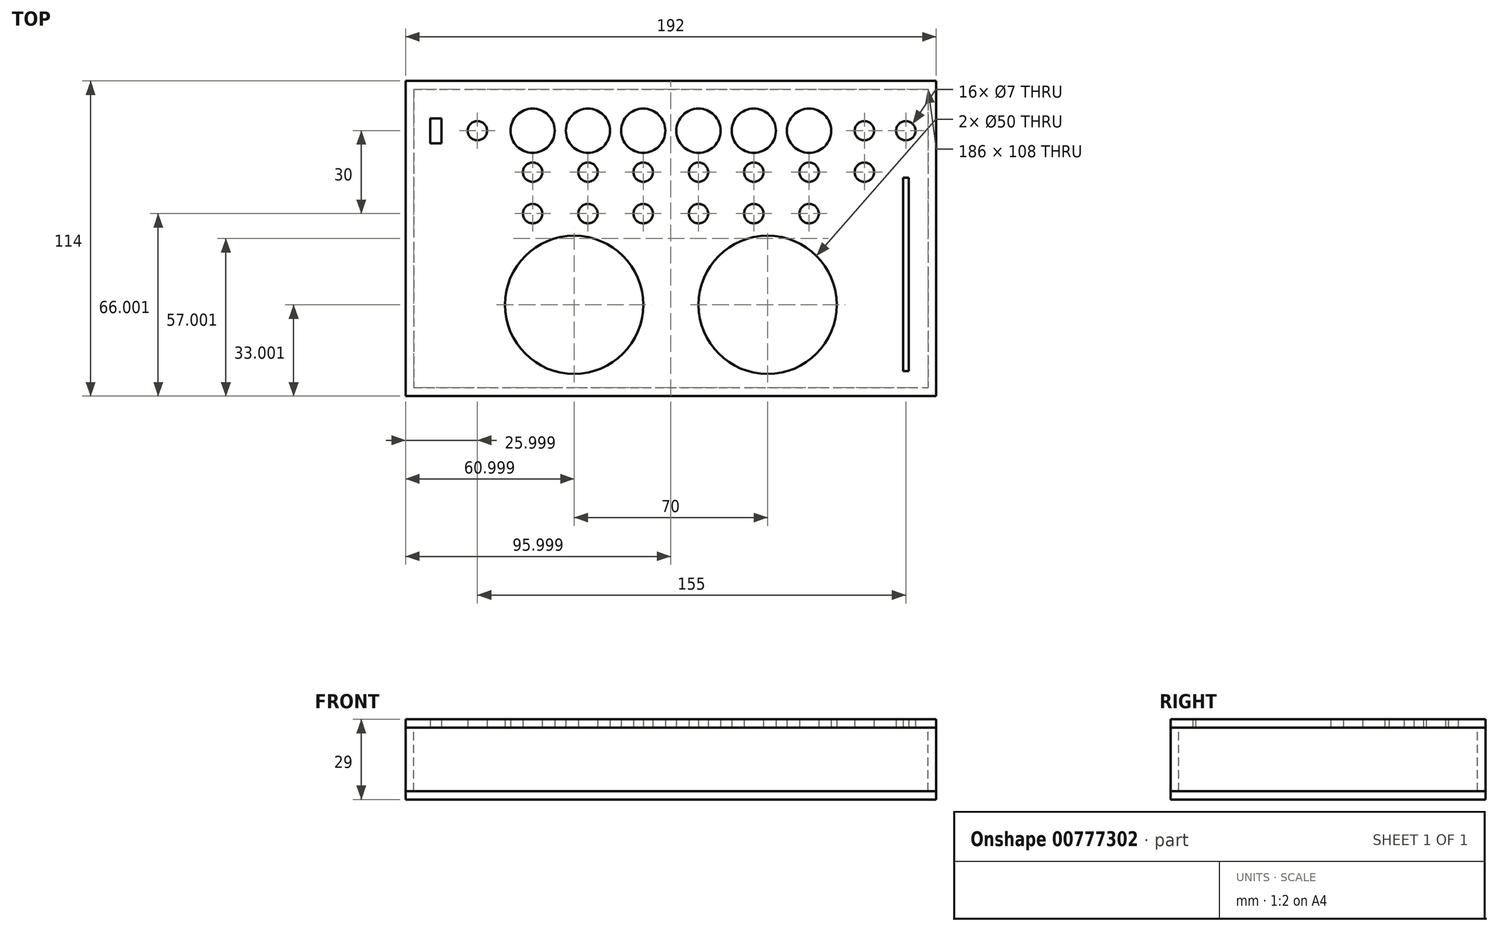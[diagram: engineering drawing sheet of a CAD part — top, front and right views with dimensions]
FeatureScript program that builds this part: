
annotation { "Feature Type Name" : "Feature", "Feature Type Description" : "" }
export const myFeature = defineFeature(function(context is Context, id is Id, definition is map)
    precondition{}
    {
        {
            assignVariable(context, id + "F0", {"name" : "Thickness", "anyValue" : 3});
        }
        {
            var Q0;
            Q0=qCreatedBy(makeId("Top.planeOp"),FACE);
            var sketch = newSketch(context, id + "F1", { "sketchPlane" : qUnion([Q0])});
            skLineSegment(sketch, "E0.bottom", {"start": v(-101.05, 57.8) * mm, "end": v(90.95, 57.8) * mm});
            skLineSegment(sketch, "E0.top", {"start": v(-101.05, -56.2) * mm, "end": v(90.95, -56.2) * mm});
            skLineSegment(sketch, "E0.left", {"start": v(-101.05, 57.8) * mm, "end": v(-101.05, -56.2) * mm});
            skLineSegment(sketch, "E0.right", {"start": v(90.95, 57.8) * mm, "end": v(90.95, -56.2) * mm});
            skLineSegment(sketch, "E1.0", {"start": v(-98.05, 54.8) * mm, "end": v(-98.05, -53.2) * mm});
            skLineSegment(sketch, "E1.1", {"start": v(-98.05, 54.8) * mm, "end": v(87.95, 54.8) * mm});
            skLineSegment(sketch, "E1.2", {"start": v(87.95, 54.8) * mm, "end": v(87.95, -53.2) * mm});
            skLineSegment(sketch, "E1.3", {"start": v(-98.05, -53.2) * mm, "end": v(87.95, -53.2) * mm});
            skLineSegment(sketch, "E2.bottom", {"start": v(73.45, -6.8) * mm, "end": v(56.45, -6.8) * mm});
            skLineSegment(sketch, "E2.top", {"start": v(73.45, 13.2) * mm, "end": v(56.45, 13.2) * mm});
            skLineSegment(sketch, "E2.left", {"start": v(73.45, -6.8) * mm, "end": v(73.45, 13.2) * mm});
            skLineSegment(sketch, "E2.right", {"start": v(56.45, -6.8) * mm, "end": v(56.45, 13.2) * mm});
            skPoint(sketch, "E2.middle", {"position": v(64.95, 3.2) * mm});
            skLineSegment(sketch, "E3.bottom", {"start": v(-88.05, 35.3) * mm, "end": v(-92.05, 35.3) * mm});
            skLineSegment(sketch, "E3.top", {"start": v(-88.05, 44.3) * mm, "end": v(-92.05, 44.3) * mm});
            skLineSegment(sketch, "E3.left", {"start": v(-88.05, 35.3) * mm, "end": v(-88.05, 44.3) * mm});
            skLineSegment(sketch, "E3.right", {"start": v(-92.05, 35.3) * mm, "end": v(-92.05, 44.3) * mm});
            skPoint(sketch, "E3.middle", {"position": v(-90.05, 39.8) * mm});
            skCircle(sketch, "E4", {"center": v(-75.05, 39.8) * mm, "radius": 3.5 * mm});
            skLineSegment(sketch, "E5.bottom", {"start": v(84.95, -49.72) * mm, "end": v(74.95, -49.72) * mm});
            skLineSegment(sketch, "E5.top", {"start": v(84.95, 25.28) * mm, "end": v(74.95, 25.28) * mm});
            skLineSegment(sketch, "E5.left", {"start": v(84.95, -49.72) * mm, "end": v(84.95, 25.28) * mm});
            skLineSegment(sketch, "E5.right", {"start": v(74.95, -49.72) * mm, "end": v(74.95, 25.28) * mm});
            skLineSegment(sketch, "E6.bottom", {"start": v(80.95, -47.22) * mm, "end": v(78.95, -47.22) * mm});
            skLineSegment(sketch, "E6.top", {"start": v(80.95, 22.78) * mm, "end": v(78.95, 22.78) * mm});
            skLineSegment(sketch, "E6.left", {"start": v(80.95, -47.22) * mm, "end": v(80.95, 22.78) * mm});
            skLineSegment(sketch, "E6.right", {"start": v(78.95, -47.22) * mm, "end": v(78.95, 22.78) * mm});
            skPoint(sketch, "E6.middle", {"position": v(79.95, -12.22) * mm});
            skCircle(sketch, "E7", {"center": v(79.95, 39.8) * mm, "radius": 3.5 * mm});
            skCircle(sketch, "E8", {"center": v(4.95, 39.8) * mm, "radius": 8 * mm});
            skCircle(sketch, "E9", {"center": v(-15.05, 39.8) * mm, "radius": 8 * mm});
            skCircle(sketch, "E10", {"center": v(24.95, 39.8) * mm, "radius": 8 * mm});
            skCircle(sketch, "E11", {"center": v(4.95, 24.8) * mm, "radius": 3.5 * mm});
            skCircle(sketch, "E12", {"center": v(44.95, 24.8) * mm, "radius": 3.5 * mm});
            skCircle(sketch, "E13", {"center": v(24.95, 24.8) * mm, "radius": 3.5 * mm});
            skCircle(sketch, "E14", {"center": v(-35.05, 24.8) * mm, "radius": 3.5 * mm});
            skCircle(sketch, "E15", {"center": v(-15.05, 24.8) * mm, "radius": 3.5 * mm});
            skCircle(sketch, "E16", {"center": v(-55.05, 24.8) * mm, "radius": 3.5 * mm});
            skCircle(sketch, "E17", {"center": v(24.95, 9.8) * mm, "radius": 3.5 * mm});
            skCircle(sketch, "E18", {"center": v(44.95, 9.8) * mm, "radius": 3.5 * mm});
            skCircle(sketch, "E19", {"center": v(4.95, 9.8) * mm, "radius": 3.5 * mm});
            skCircle(sketch, "E20", {"center": v(-35.05, 9.8) * mm, "radius": 3.5 * mm});
            skCircle(sketch, "E21", {"center": v(-15.05, 9.8) * mm, "radius": 3.5 * mm});
            skCircle(sketch, "E22", {"center": v(-55.05, 9.8) * mm, "radius": 3.5 * mm});
            skCircle(sketch, "E23", {"center": v(64.95, 39.8) * mm, "radius": 3.5 * mm});
            skCircle(sketch, "E24", {"center": v(64.95, 24.8) * mm, "radius": 3.5 * mm});
            skCircle(sketch, "E25", {"center": v(-35.05, 39.8) * mm, "radius": 8 * mm});
            skCircle(sketch, "E26", {"center": v(44.95, 39.8) * mm, "radius": 8 * mm});
            skCircle(sketch, "E27", {"center": v(-55.05, 39.8) * mm, "radius": 8 * mm});
            skCircle(sketch, "E28", {"center": v(-40.05, -23.2) * mm, "radius": 25 * mm});
            skCircle(sketch, "E29", {"center": v(29.95, -23.2) * mm, "radius": 25 * mm});
            skSolve(sketch);
        }
        {
            var Q0;
            Q0=makeQuery(id+"F1.imprint","IMPRINT",FACE,{"disambiguationData":[TD([[makeQuery(id+"F1.imprint","IMPRINT",EDGE,{"derivedFrom":sQuery(id+"F1.wireOp",EDGE,"E0.bottom")}),-1.0]])]});
            extrude(context, id + "F2", {"entities" : qUnion([Q0]), "oppositeDirection" : true, "depth" : (29 - getVariable(context, 'Thickness') * 2) * mm, "offsetDistance" : 25 * mm});
        }
        {
            var Q0;
            Q0=makeQuery(id+"F1.imprint","IMPRINT",FACE,{"disambiguationData":[TD([[makeQuery(id+"F1.imprint","IMPRINT",EDGE,{"derivedFrom":sQuery(id+"F1.wireOp",EDGE,"E0.bottom")}),-1.0]])]});
            var Q1;
            Q1=makeQuery(id+"F1.imprint","IMPRINT",FACE,{"disambiguationData":[TD([[makeQuery(id+"F1.imprint","IMPRINT",EDGE,{"derivedFrom":sQuery(id+"F1.wireOp",EDGE,"E1.0")}),1.0]])]});
            var Q2;
            Q2=makeQuery(id+"F1.imprint","IMPRINT",FACE,{"disambiguationData":[TD([[makeQuery(id+"F1.imprint","IMPRINT",EDGE,{"derivedFrom":sQuery(id+"F1.wireOp",EDGE,"E2.bottom")}),-1.0]])]});
            var Q3;
            Q3=makeQuery(id+"F1.imprint","IMPRINT",FACE,{"disambiguationData":[TD([[makeQuery(id+"F1.imprint","IMPRINT",EDGE,{"derivedFrom":sQuery(id+"F1.wireOp",EDGE,"E5.bottom")}),-1.0]])]});
            var Q4;
            Q4=makeQuery(id+"F1.imprint","IMPRINT",FACE,{"disambiguationData":[TD([[makeQuery(id+"F1.imprint","IMPRINT",EDGE,{"derivedFrom":sQuery(id+"F1.wireOp",EDGE,"1PGvYNiY-SpdE-KHsO-0nZL-MrIaACnWbyKp.bottom")}),-1.0]])]});
            extrude(context, id + "F3", {"entities" : qUnion([Q0, Q1, Q2, Q3, Q4]), "depth" : (getVariable(context, 'Thickness')) * mm, "offsetDistance" : 25 * mm});
        }
        {
            var Q0;
            Q0=makeQuery(id+"F2.opExtrude","CAP_FACE",FACE,{"disambiguationData":[OSD([sQuery(id+"F1.wireOp",EDGE,"E0.bottom"),sQuery(id+"F1.wireOp",EDGE,"E0.top"),sQuery(id+"F1.wireOp",EDGE,"E0.left"),sQuery(id+"F1.wireOp",EDGE,"E0.right"),sQuery(id+"F1.wireOp",EDGE,"E1.0"),sQuery(id+"F1.wireOp",EDGE,"E1.1"),sQuery(id+"F1.wireOp",EDGE,"E1.2"),sQuery(id+"F1.wireOp",EDGE,"E1.3")])],"isStart":false});
            var sketch = newSketch(context, id + "F4", { "sketchPlane" : qUnion([Q0])});
            skLineSegment(sketch, "E30.bottom", {"start": v(-101.05, 56.2) * mm, "end": v(90.95, 56.2) * mm});
            skLineSegment(sketch, "E30.top", {"start": v(-101.05, -57.8) * mm, "end": v(90.95, -57.8) * mm});
            skLineSegment(sketch, "E30.left", {"start": v(-101.05, 56.2) * mm, "end": v(-101.05, -57.8) * mm});
            skLineSegment(sketch, "E30.right", {"start": v(90.95, 56.2) * mm, "end": v(90.95, -57.8) * mm});
            skSolve(sketch);
        }
        {
            var Q0;
            Q0 = qSketchRegion(id + "F4", true);
            var Q1;
            Q1=makeQuery(id+"F4.imprint","IMPRINT",FACE,{"disambiguationData":[TD([[makeQuery(id+"F4.imprint","IMPRINT",EDGE,{"derivedFrom":makeQuery(id+"F2.opExtrude","CAP_EDGE",EDGE,{"disambiguationData":[OSD([sQuery(id+"F1.wireOp",EDGE,"E1.0")])],"isStart":false})}),-1.0]])]});
            extrude(context, id + "F5", {"entities" : qUnion([Q0, Q1]), "depth" : (getVariable(context, 'Thickness')) * mm, "offsetDistance" : 25 * mm});
        }
    });
